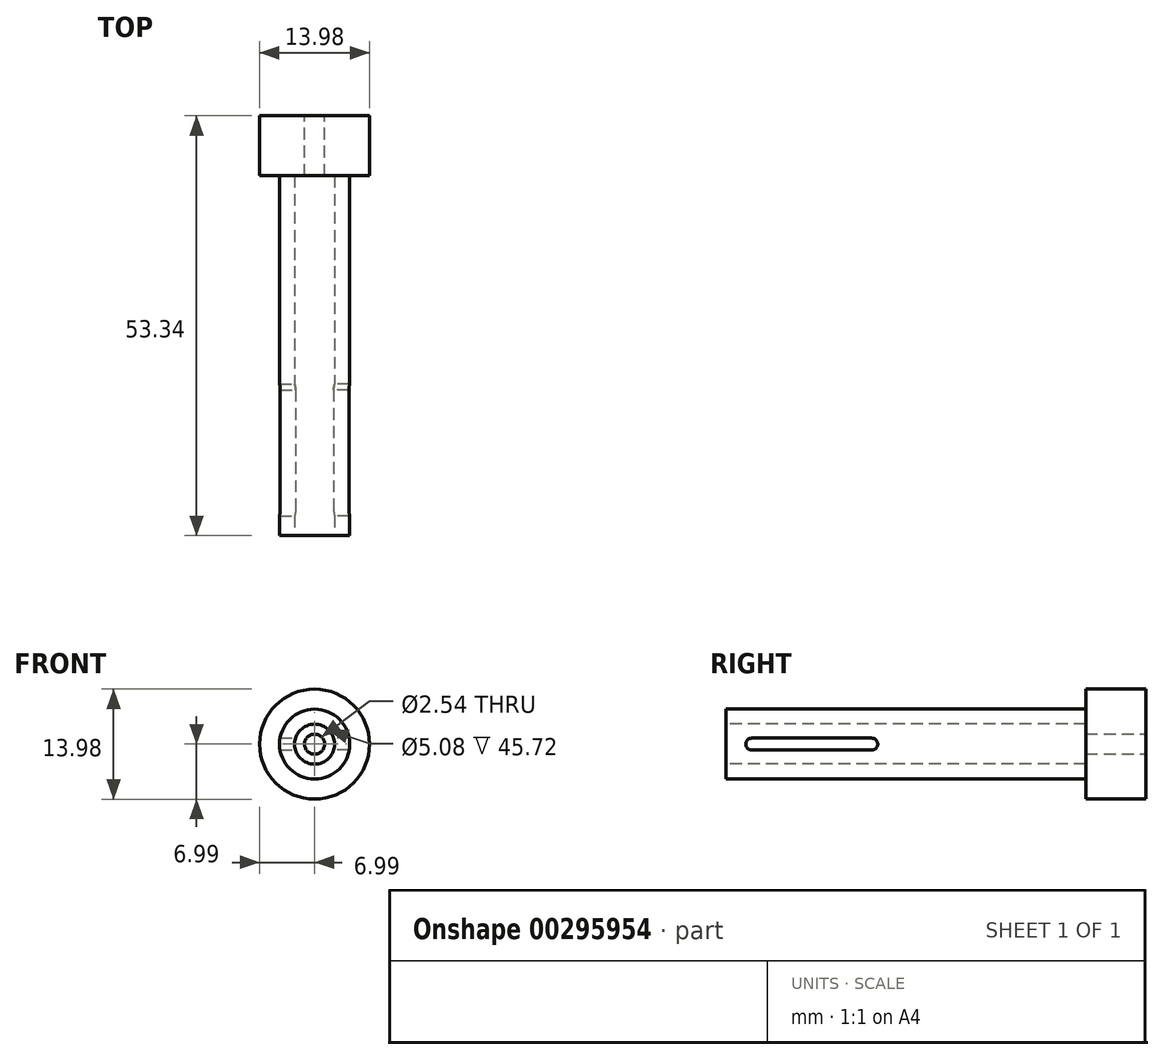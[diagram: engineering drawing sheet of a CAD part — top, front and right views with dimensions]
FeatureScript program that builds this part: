
annotation { "Feature Type Name" : "Feature", "Feature Type Description" : "" }
export const myFeature = defineFeature(function(context is Context, id is Id, definition is map)
    precondition{}
    {
        {
            var Q0;
            Q0=qCreatedBy(makeId("Front.planeOp"),FACE);
            var sketch = newSketch(context, id + "F0", { "sketchPlane" : qUnion([Q0])});
            skCircle(sketch, "E0", {"center": v(0, 0) * mm, "radius": 6.99 * mm});
            skCircle(sketch, "E1", {"center": v(0, 0) * mm, "radius": 1.27 * mm});
            skSolve(sketch);
        }
        {
            var Q0;
            Q0 = qSketchRegion(id + "F0", true);
            var Q1;
            Q1=makeQuery(id+"F0.imprint","IMPRINT",FACE,{"disambiguationData":[TD([[makeQuery(id+"F0.imprint","IMPRINT",EDGE,{"derivedFrom":sQuery(id+"F0.wireOp",EDGE,"E0")}),1.0]])]});
            extrude(context, id + "F1", {"entities" : qUnion([Q0, Q1]), "depth" : 7.62 * mm});
        }
        {
            var Q0;
            Q0=makeQuery(id+"F1.opExtrude","CAP_FACE",FACE,{"disambiguationData":[OSD([sQuery(id+"F0.wireOp",EDGE,"E0"),sQuery(id+"F0.wireOp",EDGE,"E1")])],"isStart":false});
            var sketch = newSketch(context, id + "F2", { "sketchPlane" : qUnion([Q0])});
            skCircle(sketch, "E2", {"center": v(0, 0) * mm, "radius": 4.45 * mm});
            skSolve(sketch);
        }
        {
            var Q0;
            Q0=makeQuery(id+"F2.imprint","IMPRINT",FACE,{"disambiguationData":[TD([[makeQuery(id+"F2.imprint","IMPRINT",EDGE,{"derivedFrom":sQuery(id+"F2.wireOp",EDGE,"E2")}),1.0]])]});
            extrude(context, id + "F3", {"entities" : qUnion([Q0]), "operationType" : NewBodyOperationType.ADD, "depth" : 45.72 * mm});
        }
        {
            var Q0;
            Q0=qCreatedBy(makeId("Right.planeOp"),FACE);
            var sketch = newSketch(context, id + "F4", { "sketchPlane" : qUnion([Q0])});
            skLineSegment(sketch, "E3", {"start": v(-53.35, 0) * mm, "end": v(-50.81, 0) * mm});
            skLineSegment(sketch, "E4", {"start": v(-50.81, 0) * mm, "end": v(-34.05, 0) * mm});
            skCircle(sketch, "E5", {"center": v(-34.81, 0) * mm, "radius": 0.76 * mm});
            skCircle(sketch, "E6", {"center": v(-50.05, 0) * mm, "radius": 0.76 * mm});
            skLineSegment(sketch, "E7", {"start": v(-34.83, 0.76) * mm, "end": v(-50.05, 0.76) * mm});
            skLineSegment(sketch, "E8", {"start": v(-50.05, 0.76) * mm, "end": v(-50.05, -0.76) * mm});
            skLineSegment(sketch, "E9", {"start": v(-50.05, -0.76) * mm, "end": v(-34.81, -0.76) * mm});
            skSolve(sketch);
        }
        {
            var Q0;
            Q0 = qSketchRegion(id + "F4", true);
            extrude(context, id + "F5", {"entities" : qUnion([Q0]), "operationType" : NewBodyOperationType.REMOVE, "oppositeDirection" : true, "depth" : 25.4 * mm});
        }
        {
            var Q0;
            Q0 = qSketchRegion(id + "F4", true);
            extrude(context, id + "F6", {"entities" : qUnion([Q0]), "operationType" : NewBodyOperationType.REMOVE, "depth" : 25.4 * mm});
        }
        {
            var Q0;
            Q0=makeQuery(id+"F3.opExtrude","CAP_FACE",FACE,{"disambiguationData":[OSD([sQuery(id+"F0.wireOp",EDGE,"E1"),sQuery(id+"F2.wireOp",EDGE,"E2")])],"isStart":false});
            var sketch = newSketch(context, id + "F7", { "sketchPlane" : qUnion([Q0])});
            skCircle(sketch, "E10", {"center": v(0, 0) * mm, "radius": 2.54 * mm});
            skSolve(sketch);
        }
        {
            var Q0;
            Q0=makeQuery(id+"F7.imprint","IMPRINT",FACE,{"disambiguationData":[TD([[makeQuery(id+"F7.imprint","IMPRINT",EDGE,{"derivedFrom":sQuery(id+"F7.wireOp",EDGE,"E10")}),1.0]])]});
            extrude(context, id + "F8", {"entities" : qUnion([Q0]), "operationType" : NewBodyOperationType.REMOVE, "oppositeDirection" : true, "depth" : 20.32 * mm});
        }
        {
            var Q0;
            Q0=makeQuery(id+"F8.boolean.opBoolean","COPY",FACE,{"derivedFrom":makeQuery(id+"F8.opExtrude","CAP_FACE",FACE,{"disambiguationData":[OSD([sQuery(id+"F0.wireOp",EDGE,"E1"),sQuery(id+"F7.wireOp",EDGE,"E10")])],"isStart":false})});
            extrude(context, id + "F9", {"entities" : qUnion([Q0]), "operationType" : NewBodyOperationType.REMOVE, "oppositeDirection" : true, "depth" : 25.4 * mm});
        }
    });
